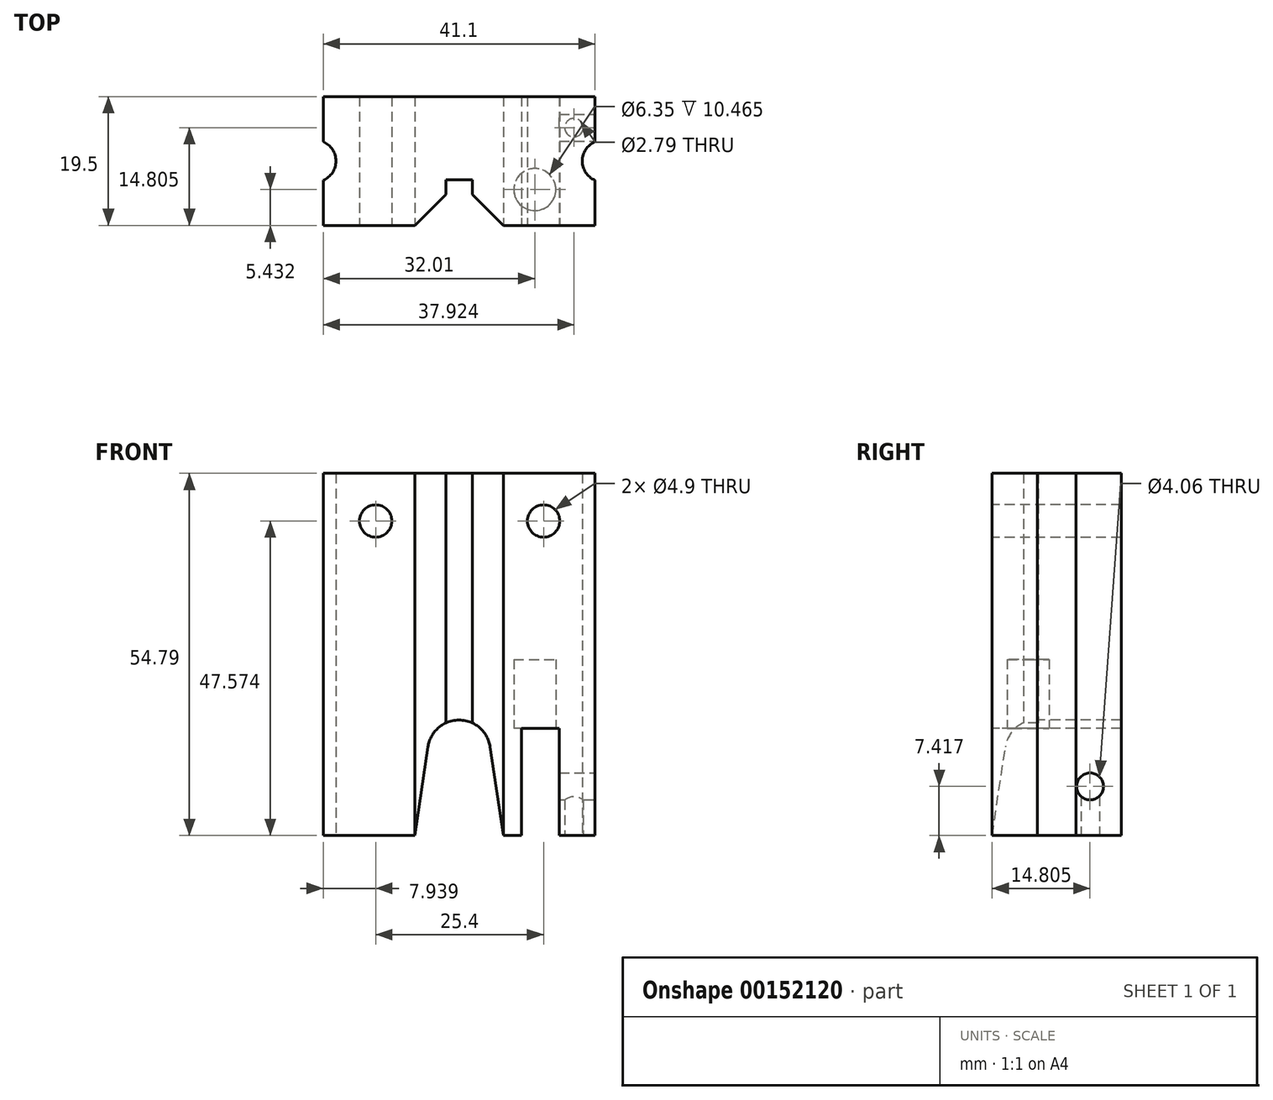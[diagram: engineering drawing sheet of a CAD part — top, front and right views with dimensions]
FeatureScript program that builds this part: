
annotation { "Feature Type Name" : "Feature", "Feature Type Description" : "" }
export const myFeature = defineFeature(function(context is Context, id is Id, definition is map)
    precondition{}
    {
        {
            var Q0;
            Q0=qCreatedBy(makeId("Top.planeOp"),FACE);
            var sketch = newSketch(context, id + "F0", { "sketchPlane" : qUnion([Q0])});
            skLineSegment(sketch, "E0.bottom", {"start": v(20.55, 9.75) * mm, "end": v(-20.55, 9.75) * mm});
            skLineSegment(sketch, "E0.top", {"start": v(20.55, -9.75) * mm, "end": v(6.7, -9.75) * mm});
            skLineSegment(sketch, "E0.left", {"start": v(20.55, 9.75) * mm, "end": v(20.55, 2.9) * mm});
            skLineSegment(sketch, "E0.right", {"start": v(-20.55, 9.75) * mm, "end": v(-20.55, 2.92) * mm});
            skPoint(sketch, "E0.middle", {"position": v(0, 0) * mm});
            skLineSegment(sketch, "E1.bottom", {"start": v(2, -2.82) * mm, "end": v(-2, -2.82) * mm});
            skLineSegment(sketch, "E1.left", {"start": v(2, -2.82) * mm, "end": v(2, -5.04) * mm});
            skLineSegment(sketch, "E1.right", {"start": v(-2, -2.82) * mm, "end": v(-2, -5.04) * mm});
            skLineSegment(sketch, "E2.trimOffspring", {"start": v(-6.7, -9.75) * mm, "end": v(-20.55, -9.75) * mm});
            skLineSegment(sketch, "E3.bottom", {"start": v(-2, -5.04) * mm, "end": v(-6.74, -9.78) * mm});
            skLineSegment(sketch, "E3.left", {"start": v(2, -5.04) * mm, "end": v(6.74, -9.78) * mm});
            skArc(sketch, "E4", {"start": v(20.55, 2.9) * mm, "mid": v(18.64, 0) * mm, "end": v(20.55, -2.9) * mm});
            skArc(sketch, "E5", {"start": v(-20.55, -2.92) * mm, "mid": v(-18.62, 0) * mm, "end": v(-20.55, 2.92) * mm});
            skLineSegment(sketch, "E6.trimOffspring", {"start": v(-20.55, -2.92) * mm, "end": v(-20.55, -9.75) * mm});
            skLineSegment(sketch, "E7.trimOffspring", {"start": v(20.55, -2.9) * mm, "end": v(20.55, -9.75) * mm});
            skSolve(sketch);
        }
        {
            var Q0;
            Q0=makeQuery(id+"F0.imprint","IMPRINT",FACE,{"disambiguationData":[TD([[makeQuery(id+"F0.imprint","IMPRINT",EDGE,{"derivedFrom":sQuery(id+"F0.wireOp",EDGE,"E0.bottom")}),1.0]])]});
            extrude(context, id + "F1", {"entities" : qUnion([Q0]), "depth" : 54.8 * mm});
        }
        {
            var Q0;
            Q0=makeQuery(id+"F1.opExtrude","SWEPT_FACE",FACE,{"disambiguationData":[OSD([sQuery(id+"F0.wireOp",EDGE,"E2.trimOffspring")])]});
            var sketch = newSketch(context, id + "F2", { "sketchPlane" : qUnion([Q0])});
            skCircle(sketch, "E8", {"center": v(-12.61, 47.57) * mm, "radius": 2.45 * mm});
            skCircle(sketch, "E9", {"center": v(12.79, 47.57) * mm, "radius": 2.45 * mm});
            skLineSegment(sketch, "E10.bottom", {"start": v(15.15, 16.18) * mm, "end": v(9.44, 16.18) * mm});
            skLineSegment(sketch, "E10.left", {"start": v(15.15, 16.18) * mm, "end": v(15.15, 0) * mm});
            skLineSegment(sketch, "E10.right", {"start": v(9.44, 16.18) * mm, "end": v(9.44, 0) * mm});
            skLineSegment(sketch, "E11", {"start": v(9.44, 0) * mm, "end": v(15.15, 0) * mm});
            skArc(sketch, "E12", {"start": v(4.71, 13.4) * mm, "mid": v(0, 17.46) * mm, "end": v(-4.71, 13.4) * mm});
            skLineSegment(sketch, "E13", {"start": v(-6.7, 0) * mm, "end": v(-4.71, 13.4) * mm});
            skLineSegment(sketch, "E14", {"start": v(4.71, 13.4) * mm, "end": v(6.7, 0) * mm});
            skLineSegment(sketch, "E15", {"start": v(-6.7, 0) * mm, "end": v(6.7, 0) * mm});
            skSolve(sketch);
        }
        {
            var Q0;
            Q0 = qSketchRegion(id + "F2", true);
            extrude(context, id + "F3", {"entities" : qUnion([Q0]), "operationType" : NewBodyOperationType.REMOVE, "oppositeDirection" : true, "depth" : 25.4 * mm});
        }
        {
            var Q0;
            Q0=makeQuery(id+"F3.boolean.opBoolean","COPY",FACE,{"derivedFrom":makeQuery(id+"F3.opExtrude","SWEPT_FACE",FACE,{"disambiguationData":[OSD([sQuery(id+"F2.wireOp",EDGE,"E10.bottom")])]})});
            var sketch = newSketch(context, id + "F4", { "sketchPlane" : qUnion([Q0])});
            skCircle(sketch, "E16", {"center": v(11.46, 4.32) * mm, "radius": 3.17 * mm});
            skSolve(sketch);
        }
        {
            var Q0;
            Q0 = qSketchRegion(id + "F4", true);
            extrude(context, id + "F5", {"entities" : qUnion([Q0]), "operationType" : NewBodyOperationType.REMOVE, "oppositeDirection" : true, "depth" : 10.46 * mm});
        }
        {
            var Q0;
            Q0=makeQuery(id+"F1.opExtrude","SWEPT_FACE",FACE,{"disambiguationData":[OSD([sQuery(id+"F0.wireOp",EDGE,"E0.left")])]});
            var sketch = newSketch(context, id + "F6", { "sketchPlane" : qUnion([Q0])});
            skCircle(sketch, "E17", {"center": v(5.05, 7.42) * mm, "radius": 2.03 * mm});
            skSolve(sketch);
        }
        {
            var Q0;
            Q0 = qSketchRegion(id + "F6", true);
            extrude(context, id + "F7", {"entities" : qUnion([Q0]), "operationType" : NewBodyOperationType.REMOVE, "endBound" : BoundingType.UP_TO_NEXT, "oppositeDirection" : true, "depth" : 6.35 * mm});
        }
        {
            var Q0;
            {var subQ0=sQuery(id+"F0.wireOp",EDGE,"E4");var subQ1=sQuery(id+"F0.wireOp",EDGE,"E0.left");var subQ2=sQuery(id+"F0.wireOp",EDGE,"E0.top");var subQ3=sQuery(id+"F0.wireOp",EDGE,"E0.bottom");var subQ4=sQuery(id+"F0.wireOp",EDGE,"E7.trimOffspring");Q0=makeQuery(id+"F3.boolean.opBoolean","SPLIT",FACE,{"disambiguationData":[TD([makeQuery(id+"F1.opExtrude","SWEPT_FACE",FACE,{"disambiguationData":[OSD([subQ1])]})])],"derivedFrom":makeQuery(id+"F1.opExtrude","CAP_FACE",FACE,{"disambiguationData":[OSD([subQ3,subQ2,subQ1,sQuery(id+"F0.wireOp",EDGE,"E0.right"),sQuery(id+"F0.wireOp",EDGE,"E1.bottom"),sQuery(id+"F0.wireOp",EDGE,"E1.left"),sQuery(id+"F0.wireOp",EDGE,"E1.right"),sQuery(id+"F0.wireOp",EDGE,"E2.trimOffspring"),sQuery(id+"F0.wireOp",EDGE,"E3.bottom"),sQuery(id+"F0.wireOp",EDGE,"E3.left"),subQ0,sQuery(id+"F0.wireOp",EDGE,"E5"),sQuery(id+"F0.wireOp",EDGE,"E6.trimOffspring"),subQ4])],"isStart":true})});}
            var sketch = newSketch(context, id + "F8", { "sketchPlane" : qUnion([Q0])});
            skCircle(sketch, "E18", {"center": v(17.37, -5.05) * mm, "radius": 1.4 * mm});
            skSolve(sketch);
        }
        {
            var Q0;
            Q0 = qSketchRegion(id + "F8", true);
            extrude(context, id + "F9", {"entities" : qUnion([Q0]), "operationType" : NewBodyOperationType.REMOVE, "endBound" : BoundingType.UP_TO_NEXT, "oppositeDirection" : true, "depth" : 25.4 * mm});
        }
    });
